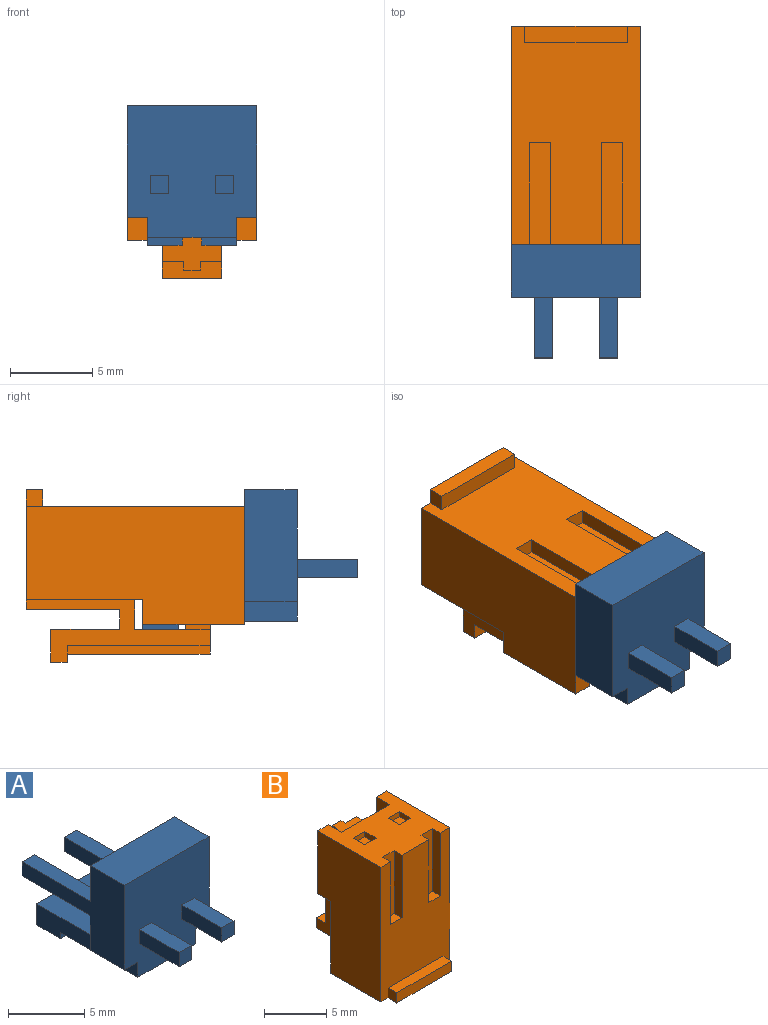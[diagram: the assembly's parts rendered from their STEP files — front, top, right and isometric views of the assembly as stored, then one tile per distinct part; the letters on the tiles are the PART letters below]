
ASSEMBLY  parts=2 mates=1
PART A: 34 faces, bbox 7.9x14.6x8.5 mm
  f0: plane 7.7x1.14mm, normal (0,0,1), area 8.8mm2, adj f1,f2,f3,f4
  f1: plane 1.14x1.14mm, normal (0,1,0), area 1.3mm2, adj f0,f2,f3,f5
  f2: plane 7.7x1.14mm, normal (-1,0,0), area 8.8mm2, adj f0,f1,f4,f5
  f3: plane 7.7x1.14mm, normal (1,0,0), area 8.8mm2, adj f0,f1,f4,f5
  f4: plane 7.86x6.8mm, normal (0,1,0), area 50.8mm2, adj f0,f2,f3,f5,f6,f7,f8,f9
  f5: plane 7.7x1.14mm, normal (0,0,-1), area 8.8mm2, adj f1,f2,f3,f4
  f6: plane 3.2x1.25mm, normal (0,0,-1), area 4mm2, adj f4,f11,f16,f17
  f7: plane 7.7x1.14mm, normal (0,0,-1), area 8.8mm2, adj f4,f8,f12,f18
  f8: plane 7.7x1.14mm, normal (-1,0,0), area 8.8mm2, adj f4,f7,f13,f18
  f9: plane 3.2x1.25mm, normal (0,0,-1), area 4mm2, adj f4,f14,f17,f19
  f10: plane 7.86x3.2mm, normal (0,0,1), area 25.2mm2, adj f4,f11,f14,f17
  f11: plane 6.8x3.2mm, normal (1,0,0), area 21.8mm2, adj f4,f6,f10,f17
  f12: plane 7.7x1.14mm, normal (1,0,0), area 8.8mm2, adj f4,f7,f13,f18
  f13: plane 7.7x1.14mm, normal (0,0,1), area 8.8mm2, adj f4,f8,f12,f18
  f14: plane 6.8x3.2mm, normal (-1,0,0), area 21.8mm2, adj f4,f9,f10,f17
  f15: plane 6.2x5.36mm, normal (0,0,1), area 33.2mm2, adj f4,f16,f19,f20
  f16: plane 9.4x1.7mm, normal (1,0,0), area 12.4mm2, adj f6,f15,f17,f20,f21,f22,f23
  f17: plane 8x7.86mm, normal (0,-1,0), area 57.3mm2, adj f6,f9,f10,f11,f14,f16,f19,f22
  f18: plane 1.14x1.14mm, normal (0,1,0), area 1.3mm2, adj f7,f8,f12,f13
  f19: plane 9.4x1.7mm, normal (-1,0,0), area 12.4mm2, adj f9,f15,f17,f20,f21,f22,f23
  f20: plane 5.36x1.7mm, normal (0,1,0), area 9.1mm2, adj f15,f16,f19,f23
  f21: plane 5.36x0.5mm, normal (0,-1,0), area 2.7mm2, adj f16,f19,f22,f23
  f22: plane 7.2x5.36mm, normal (0,0,-1), area 38.6mm2, adj f16,f17,f19,f21
  f23: plane 5.36x2.2mm, normal (0,0,-1), area 11.8mm2, adj f16,f19,f20,f21
  f24: plane 3.7x1.14mm, normal (0,0,-1), area 4.2mm2, adj f17,f25,f26,f32
  f25: plane 3.7x1.14mm, normal (-1,0,0), area 4.2mm2, adj f17,f24,f29,f32
  f26: plane 3.7x1.14mm, normal (1,0,0), area 4.2mm2, adj f17,f24,f29,f32
  f27: plane 3.7x1.14mm, normal (0,0,-1), area 4.2mm2, adj f17,f28,f30,f33
  f28: plane 3.7x1.14mm, normal (-1,0,0), area 4.2mm2, adj f17,f27,f31,f33
  f29: plane 3.7x1.14mm, normal (0,0,1), area 4.2mm2, adj f17,f25,f26,f32
  f30: plane 3.7x1.14mm, normal (1,0,0), area 4.2mm2, adj f17,f27,f31,f33
  f31: plane 3.7x1.14mm, normal (0,0,1), area 4.2mm2, adj f17,f28,f30,f33
  f32: plane 1.14x1.14mm, normal (0,-1,0), area 1.3mm2, adj f24,f25,f26,f29
  f33: plane 1.14x1.14mm, normal (0,-1,0), area 1.3mm2, adj f27,f28,f30,f31
PART B: 68 faces, bbox 7.9x10.5x13.3 mm
  f0: plane 1.3x0.9mm, normal (0,0,1), area 1.2mm2, adj f1,f2,f3,f4
  f1: plane 6.2x0.9mm, normal (-1,0,0), area 5.6mm2, adj f0,f3,f4,f5
  f2: plane 6.2x0.9mm, normal (1,0,0), area 5.6mm2, adj f0,f3,f4,f5
  f3: plane 13.3x7.86mm, normal (0,-1,0), area 82.2mm2, adj f0,f1,f2,f5,f6,f7,f8,f9
  f4: plane 6.2x1.3mm, normal (0,-1,0), area 8.1mm2, adj f0,f1,f2,f5
  f5: plane 7.86x7.2mm, normal (0,0,1), area 42.7mm2, adj f1,f2,f3,f4,f7,f11,f12,f14
  f6: plane 6.26x1mm, normal (0,0,1), area 6.3mm2, adj f3,f9,f13,f29
  f7: plane 6.2x0.9mm, normal (1,0,0), area 5.6mm2, adj f3,f5,f8,f22
  f8: plane 1.3x0.9mm, normal (0,0,1), area 1.2mm2, adj f3,f7,f12,f22
  f9: plane 1x1mm, normal (-1,0,0), area 1mm2, adj f3,f6,f10,f29
  f10: plane 7.86x7.3mm, normal (0,0,-1), area 27.9mm2, adj f3,f9,f11,f13,f14,f20,f29,f30
  f11: plane 13.3x7.2mm, normal (1,0,0), area 85.1mm2, adj f3,f5,f10,f20,f21,f44
  f12: plane 6.2x0.9mm, normal (-1,0,0), area 5.6mm2, adj f3,f5,f8,f22
  f13: plane 1x1mm, normal (1,0,0), area 1mm2, adj f3,f6,f10,f29
  f14: plane 13.3x7.2mm, normal (-1,0,0), area 85.1mm2, adj f3,f5,f10,f15,f20,f45
  f15: plane 6.2x1.2mm, normal (0,1,0), area 7.4mm2, adj f5,f14,f27,f45
  f16: plane 1.3x0.5mm, normal (-1,0,0), area 0.6mm2, adj f5,f19,f23,f46
  f17: plane 1.3x0.5mm, normal (0,-1,0), area 0.6mm2, adj f5,f18,f24,f47
  f18: plane 1.3x0.5mm, normal (1,0,0), area 0.6mm2, adj f5,f17,f25,f47
  f19: plane 1.3x0.5mm, normal (0,1,0), area 0.6mm2, adj f5,f16,f26,f46
  f20: plane 13.3x7.86mm, normal (0,1,0), area 73.8mm2, adj f5,f10,f11,f14,f27,f28,f33,f36
  f21: plane 6.2x1.2mm, normal (0,1,0), area 7.4mm2, adj f5,f11,f28,f44
  f22: plane 6.2x1.3mm, normal (0,-1,0), area 8.1mm2, adj f5,f7,f8,f12
  f23: plane 1.3x0.5mm, normal (0,-1,0), area 0.6mm2, adj f5,f16,f26,f46
  f24: plane 1.3x0.5mm, normal (-1,0,0), area 0.6mm2, adj f5,f17,f25,f47
  f25: plane 1.3x0.5mm, normal (0,1,0), area 0.6mm2, adj f5,f18,f24,f47
  f26: plane 1.3x0.5mm, normal (1,0,0), area 0.6mm2, adj f5,f19,f23,f46
  f27: plane 6.2x1.5mm, normal (1,0,0), area 9.3mm2, adj f5,f15,f20,f45
  f28: plane 6.2x1.5mm, normal (-1,0,0), area 9.3mm2, adj f5,f20,f21,f44
  f29: plane 6.26x1mm, normal (0,-1,0), area 6.3mm2, adj f6,f9,f10,f13
  f30: plane 5.7x1.2mm, normal (0,1,0), area 6.8mm2, adj f10,f33,f37,f50
  f31: plane 3.15x0.5mm, normal (0,1,0), area 1.6mm2, adj f10,f35,f38,f51
  f32: plane 3.15x0.5mm, normal (0,-1,0), area 1.6mm2, adj f10,f35,f38,f51
  f33: plane 6.6x1.8mm, normal (-1,0,0), area 5mm2, adj f10,f20,f30,f48,f50,f52
  f34: plane 3.9x0.5mm, normal (1,0,0), area 1.9mm2, adj f10,f39,f42,f53
  f35: plane 3.9x0.5mm, normal (1,0,0), area 1.9mm2, adj f10,f31,f32,f51
  f36: plane 11.2x3.8mm, normal (-1,0,0), area 15.7mm2, adj f10,f20,f41,f49,f52,f54,f55,f56
  f37: plane 11.2x3.8mm, normal (1,0,0), area 15.7mm2, adj f10,f20,f30,f48,f50,f52,f54,f55
  f38: plane 3.9x0.5mm, normal (-1,0,0), area 1.9mm2, adj f10,f31,f32,f51
  f39: plane 3.15x0.5mm, normal (0,1,0), area 1.6mm2, adj f10,f34,f43,f53
  f40: plane 6.6x1.8mm, normal (1,0,0), area 5mm2, adj f10,f20,f41,f49,f52,f57
  f41: plane 5.7x1.2mm, normal (0,1,0), area 6.8mm2, adj f10,f36,f40,f57
  f42: plane 3.15x0.5mm, normal (0,-1,0), area 1.6mm2, adj f10,f34,f43,f53
  f43: plane 3.9x0.5mm, normal (-1,0,0), area 1.9mm2, adj f10,f39,f42,f53
  f44: plane 1.5x1.2mm, normal (0,0,-1), area 1.8mm2, adj f11,f20,f21,f28
  f45: plane 1.5x1.2mm, normal (0,0,-1), area 1.8mm2, adj f14,f15,f20,f27
  f46: plane 1.3x1.3mm, normal (0,0,1), area 1.7mm2, adj f16,f19,f23,f26
  f47: plane 1.3x1.3mm, normal (0,0,1), area 1.7mm2, adj f17,f18,f24,f25
  f48: plane 1.8x1.2mm, normal (0,0,1), area 2.2mm2, adj f20,f33,f37,f52
  f49: plane 1.8x1.2mm, normal (0,0,1), area 2.2mm2, adj f20,f36,f40,f52
  f50: plane 1.2x1.2mm, normal (0,0,-1), area 1.4mm2, adj f30,f33,f37,f52
  f51: plane 3.9x3.15mm, normal (0,0,-1), area 12.3mm2, adj f31,f32,f35,f38
  f52: plane 9.7x3.6mm, normal (0,-1,0), area 31mm2, adj f33,f36,f37,f40,f48,f49,f50,f56
  f53: plane 3.9x3.15mm, normal (0,0,-1), area 12.3mm2, adj f34,f39,f42,f43
  f54: plane 3.6x1mm, normal (0,0,1), area 3.1mm2, adj f36,f37,f55,f58,f60,f64,f65,f66
  f55: plane 3.6x1mm, normal (0,1,0), area 3.6mm2, adj f36,f37,f54,f56
  f56: plane 3.6x2mm, normal (0,0,-1), area 7.2mm2, adj f36,f37,f52,f55
  f57: plane 1.2x1.2mm, normal (0,0,-1), area 1.4mm2, adj f36,f40,f41,f52
  f58: plane 8.7x1.3mm, normal (0,1,0), area 11.3mm2, adj f36,f54,f59,f66
  f59: plane 3.6x2.1mm, normal (0,0,1), area 4.8mm2, adj f36,f37,f52,f58,f60,f62,f63,f64
  f60: plane 8.7x1.3mm, normal (0,1,0), area 11.3mm2, adj f37,f54,f59,f65
  f61: plane 1.2x0.6mm, normal (0,0,-1), area 0.7mm2, adj f52,f62,f63,f67
  f62: plane 1.5x0.6mm, normal (-1,0,0), area 0.9mm2, adj f52,f59,f61,f67
  f63: plane 1.5x0.6mm, normal (1,0,0), area 0.9mm2, adj f52,f59,f61,f67
  f64: plane 8.7x1mm, normal (0,1,0), area 8.7mm2, adj f54,f59,f65,f66
  f65: plane 8.7x0.5mm, normal (1,0,0), area 4.3mm2, adj f54,f59,f60,f64
  f66: plane 8.7x0.5mm, normal (-1,0,0), area 4.3mm2, adj f54,f58,f59,f64
  f67: plane 1.5x1.2mm, normal (0,-1,0), area 1.8mm2, adj f59,f61,f62,f63
PLACE A at identity fixed
PLACE B rot(axis=(0,-0.71,0.71),180deg) t=(0,9.85,3.25)mm
MATE fastened B.f5 <-> A.f4  axis (0,-1,0) through (-1.98,3.2,-0.55)mm
